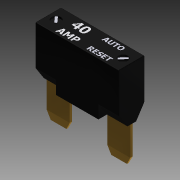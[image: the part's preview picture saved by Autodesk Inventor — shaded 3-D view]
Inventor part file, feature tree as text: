
AUTODESK INVENTOR PART (.ipt)
format: ipt  version: 2018 (Build 220112000, 112)  size: 500,736 bytes
history: native  units: in
note: dims shown in document units (in); Inventor stores cm internally (conversion verified against a paired STEP export)
features: sketch x7, chamfer x6, extrude x5, plane x5, mirror x4, emboss x2, split x1, fillet x1
ambient origin geometry x8: Origin, YZ Plane, XZ Plane, XY Plane, X Axis, Y Axis, Z Axis, Center Point
bodies: Solid1 (feature_tree)
feature tree (31):
  extrude  "Extrusion1"  Depth=0.72in
  extrude  "Extrusion2"  Depth=0.18in
  plane  "Work Plane1"
  mirror  "Mirror1"
  plane  "Work Plane2"
  mirror  "Mirror2"
  extrude  "Extrusion4"  Depth=0.28in TaperAngle=0.0deg
  chamfer  "Chamfer1"  Distance=0.49in
  chamfer  "Chamfer2"  Distance=0.1in Angle=45.0deg
  chamfer  "Chamfer3"  Distance=0.1in Angle=45.0deg
  chamfer  "Chamfer4"  Distance=0.1in Angle=45.0deg
  plane  "Work Plane3"
  mirror  "Mirror3"
  chamfer  "Chamfer5"  Distance=0.1in Angle=45.0deg
  chamfer  "Chamfer6"  Distance=0.05in Angle=45.0deg
  split  "Split1"
  extrude  "Extrusion5"  Depth=0.03in
  plane  "Work Plane4"
  emboss  "Emboss1"
  fillet  "Fillet1"  Radius=0.025in
  plane  "Work Plane5"
  emboss  "Emboss4"
  extrude  "Extrusion7"  Depth=0.03in
  mirror  "Mirror4"
  sketch  "Sketch1"  dims[d0=1.14in d1=0.72in]
  sketch  "Sketch2"  dims[d2=0.35in d3=0.0in d4=0.18in]
  sketch  "Sketch4"  dims[d5=0.1167in d6=0.28in d7=0.0in]
  sketch  "Sketch5"  dims[d13=0.315in]
  sketch  "Sketch6"  dims[d14=0.032in d15=0.49in d16=0.0in d17=0.1in d18=0.05in d19=45.0deg d20=0.1in d21=0.05in d22=45.0deg d23=0.1in d24=0.005in d25=45.0deg d26=0.1in d27=0.005in d28=45.0deg]
  sketch  "Sketch9"  dims[d29=0.0in d30=0.05in d31=0.1in d32=45.0deg]
  sketch  "Sketch10"  dims[d33=0.05in d34=0.1in d35=45.0deg d36=0.125in d37=0.025in d38=0.0in d39=0.1875in d41=0.001in d42=0.0in d43=0.01in d50=0.125in d51=0.0001in d52=0.0in d53=0.03in d56=1.0in d57=0.0in d58=0.456in d59=0.456in]
